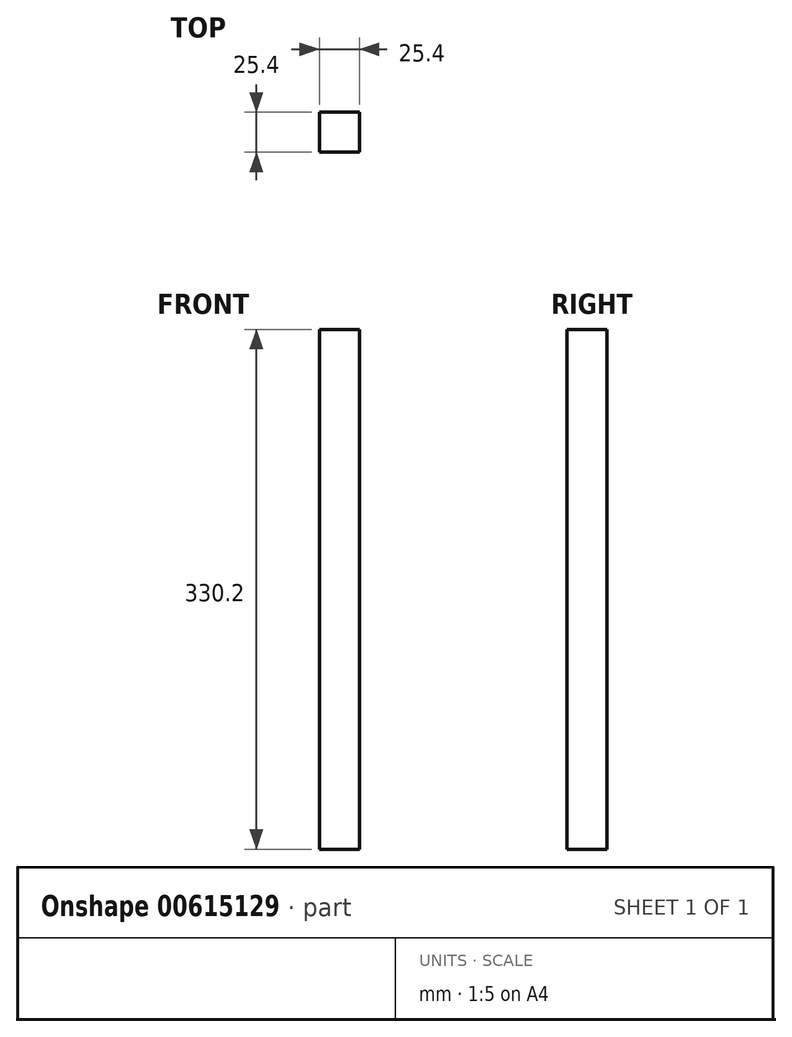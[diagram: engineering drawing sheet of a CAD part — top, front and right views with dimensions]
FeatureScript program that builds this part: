
annotation { "Feature Type Name" : "Feature", "Feature Type Description" : "" }
export const myFeature = defineFeature(function(context is Context, id is Id, definition is map)
    precondition{}
    {
        {
            var Q0;
            Q0=qCreatedBy(makeId("Right.planeOp"),FACE);
            var sketch = newSketch(context, id + "F0", { "sketchPlane" : qUnion([Q0])});
            skLineSegment(sketch, "E0.bottom", {"start": v(-7.91, 106.99) * mm, "end": v(17.49, 106.99) * mm});
            skLineSegment(sketch, "E0.top", {"start": v(-7.91, -223.21) * mm, "end": v(17.49, -223.21) * mm});
            skLineSegment(sketch, "E0.left", {"start": v(-7.91, 106.99) * mm, "end": v(-7.91, -223.21) * mm});
            skLineSegment(sketch, "E0.right", {"start": v(17.49, 106.99) * mm, "end": v(17.49, -223.21) * mm});
            skSolve(sketch);
        }
        {
            var Q0;
            Q0=qSketchRegion(id+"F0",true);
            extrude(context, id + "F1", {"entities" : qUnion([Q0]), "depth" : 25.4 * mm});
        }
    });
